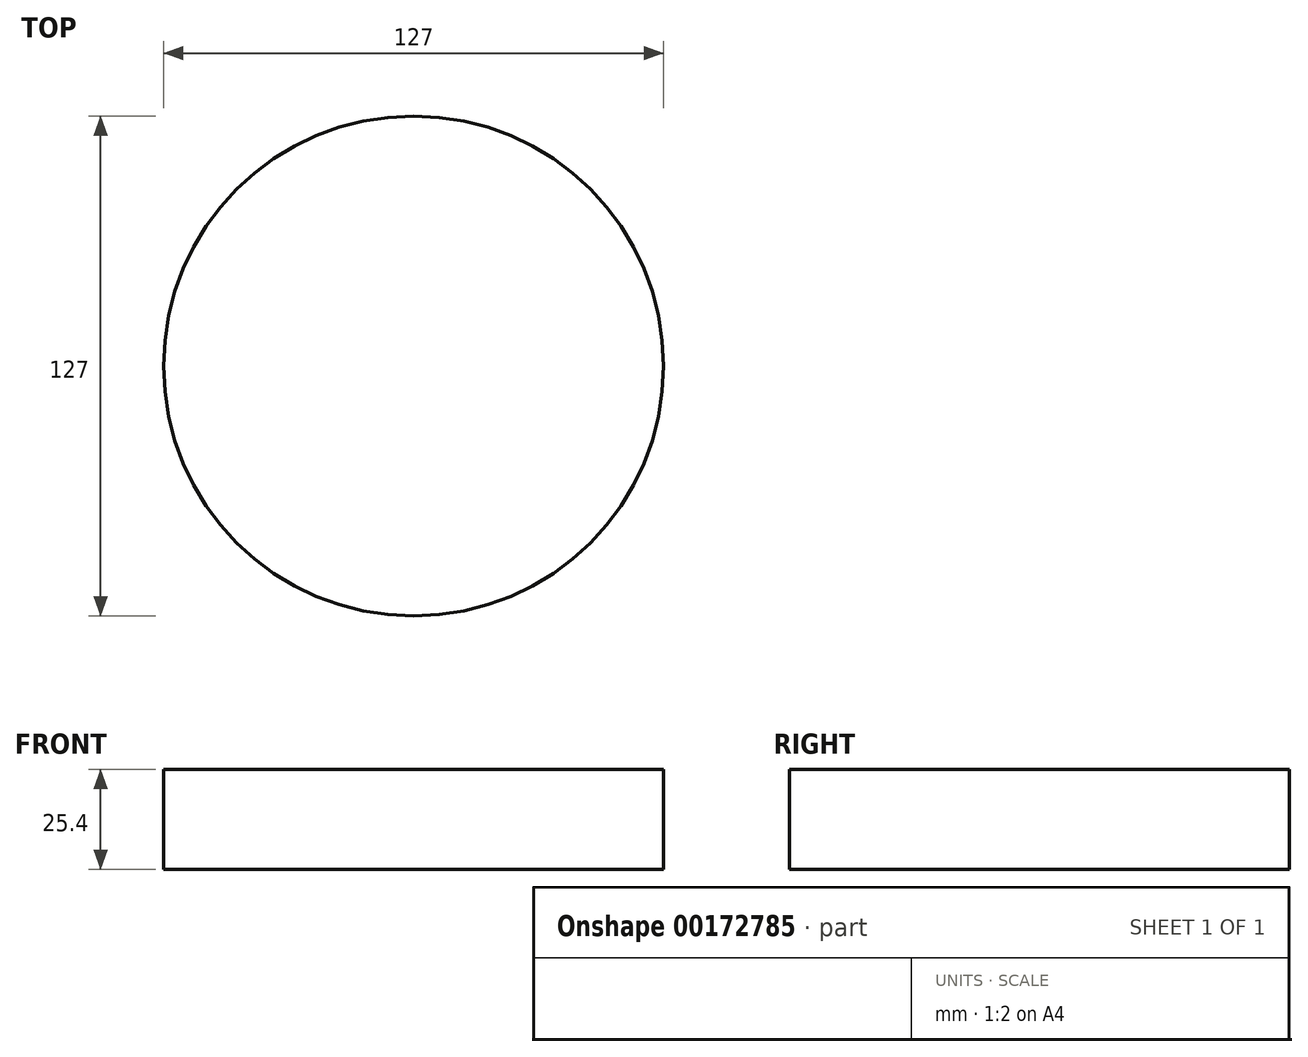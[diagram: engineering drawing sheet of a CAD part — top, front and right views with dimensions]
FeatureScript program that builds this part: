
annotation { "Feature Type Name" : "Feature", "Feature Type Description" : "" }
export const myFeature = defineFeature(function(context is Context, id is Id, definition is map)
    precondition{}
    {
        {
            var Q0;
            Q0=qCreatedBy(makeId("Top.planeOp"),FACE);
            var sketch = newSketch(context, id + "F0", { "sketchPlane" : qUnion([Q0])});
            skCircle(sketch, "E0", {"center": v(0, 0) * mm, "radius": 63.5 * mm});
            skSolve(sketch);
        }
        {
            var Q0;
            Q0=makeQuery(id+"F0.imprint","IMPRINT",FACE,{"disambiguationData":[TD([[makeQuery(id+"F0.imprint","IMPRINT",EDGE,{"derivedFrom":sQuery(id+"F0.wireOp",EDGE,"E0")}),1.0]])]});
            extrude(context, id + "F1", {"entities" : qUnion([Q0]), "depth" : 25.4 * mm});
        }
        {
            var Q0;
            Q0=qCreatedBy(makeId("Top.planeOp"),FACE);
            var sketch = newSketch(context, id + "F2", { "sketchPlane" : qUnion([Q0])});
            skLineSegment(sketch, "E1.bottom", {"start": v(-38.1, -38.1) * mm, "end": v(38.1, -38.1) * mm});
            skLineSegment(sketch, "E1.top", {"start": v(-38.1, 38.1) * mm, "end": v(38.1, 38.1) * mm});
            skLineSegment(sketch, "E1.left", {"start": v(-38.1, -38.1) * mm, "end": v(-38.1, 38.1) * mm});
            skLineSegment(sketch, "E1.right", {"start": v(38.1, -38.1) * mm, "end": v(38.1, 38.1) * mm});
            skPoint(sketch, "E1.middle", {"position": v(0, 0) * mm});
            skCircle(sketch, "E2", {"center": v(0, 0) * mm, "radius": 38.1 * mm});
            skSolve(sketch);
        }
        {
            var Q0;
            {var subQ0=sQuery(id+"F2.wireOp",EDGE,"E2");var subQ1=makeQuery(id+"F2.imprint","INTERSECT",VERTEX,{"derivedFrom":[sQuery(id+"F2.wireOp",EDGE,"E1.top"),subQ0]});Q0=makeQuery(id+"F2.imprint","IMPRINT",FACE,{"disambiguationData":[TD([[makeQuery(id+"F2.imprint","IMPRINT",EDGE,{"disambiguationData":[TD([[subQ1,1.0]])],"derivedFrom":subQ0}),1.0]])]});}
            extrude(context, id + "F3", {"entities" : qUnion([Q0]), "operationType" : NewBodyOperationType.REMOVE, "endBound" : BoundingType.THROUGH_ALL, "oppositeDirection" : true, "depth" : 25.4 * mm});
        }
    });
